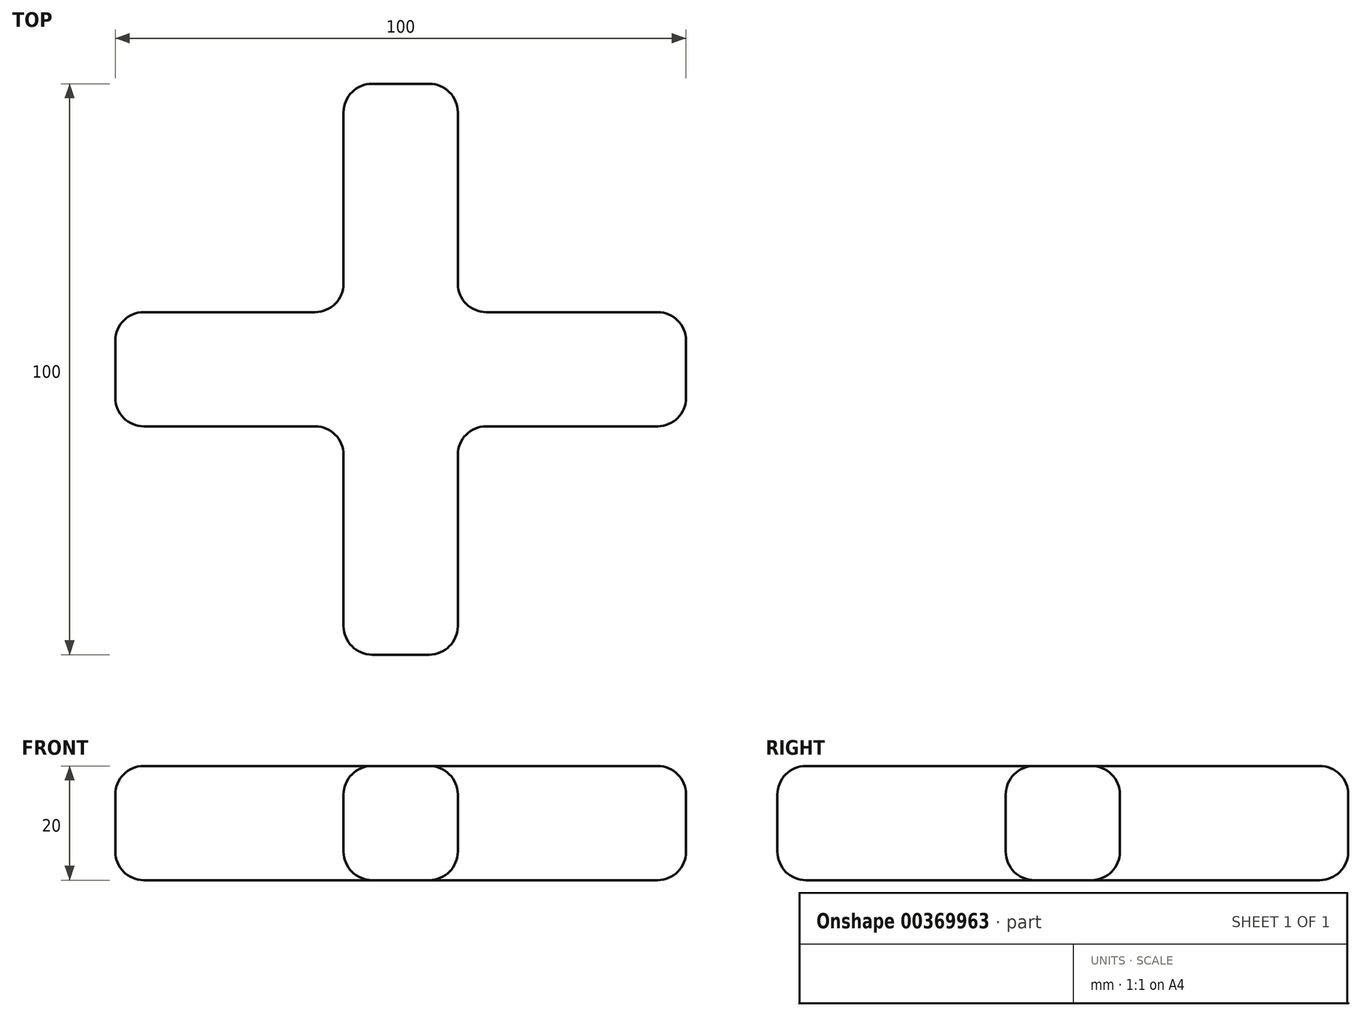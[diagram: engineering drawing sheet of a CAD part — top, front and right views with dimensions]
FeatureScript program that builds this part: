
annotation { "Feature Type Name" : "Feature", "Feature Type Description" : "" }
export const myFeature = defineFeature(function(context is Context, id is Id, definition is map)
    precondition{}
    {
        {
            var Q0;
            Q0=qCreatedBy(makeId("Top.planeOp"),FACE);
            var sketch = newSketch(context, id + "F0", { "sketchPlane" : qUnion([Q0])});
            skLineSegment(sketch, "E0.bottom", {"start": v(5, -50) * mm, "end": v(-5, -50) * mm});
            skLineSegment(sketch, "E0.top", {"start": v(5, 50) * mm, "end": v(-5, 50) * mm});
            skLineSegment(sketch, "E0.left", {"start": v(10, -45) * mm, "end": v(10, -15) * mm});
            skLineSegment(sketch, "E0.right", {"start": v(-10, 15) * mm, "end": v(-10, 45) * mm});
            skPoint(sketch, "E0.middle", {"position": v(0, 0) * mm});
            skLineSegment(sketch, "E1.bottom", {"start": v(15, -10) * mm, "end": v(45, -10) * mm});
            skLineSegment(sketch, "E1.top", {"start": v(-45, 10) * mm, "end": v(-15, 10) * mm});
            skLineSegment(sketch, "E1.left", {"start": v(-50, -5) * mm, "end": v(-50, 5) * mm});
            skLineSegment(sketch, "E1.right", {"start": v(50, -5) * mm, "end": v(50, 5) * mm});
            skPoint(sketch, "E2.newPointA", {"position": v(50, 10) * mm});
            skArc(sketch, "E2.filletArc", {"start": v(-15, 10) * mm, "mid": v(-11.46, 11.46) * mm, "end": v(-10, 15) * mm});
            skPoint(sketch, "E3.newPointA", {"position": v(-50, -10) * mm});
            skPoint(sketch, "E3.newPointB", {"position": v(10, 50) * mm});
            skArc(sketch, "E3.filletArc", {"start": v(15, -10) * mm, "mid": v(11.46, -11.46) * mm, "end": v(10, -15) * mm});
            skLineSegment(sketch, "E4", {"start": v(10, 45) * mm, "end": v(10, 15) * mm});
            skLineSegment(sketch, "E5", {"start": v(15, 10) * mm, "end": v(45, 10) * mm});
            skLineSegment(sketch, "E6", {"start": v(-45, -10) * mm, "end": v(-15, -10) * mm});
            skLineSegment(sketch, "E7", {"start": v(-10, -15) * mm, "end": v(-10, -45) * mm});
            skPoint(sketch, "E8.visualSharp", {"position": v(-10, -10) * mm});
            skArc(sketch, "E8.filletArc", {"start": v(-10, -15) * mm, "mid": v(-11.46, -11.46) * mm, "end": v(-15, -10) * mm});
            skPoint(sketch, "E9.visualSharp", {"position": v(10, 10) * mm});
            skArc(sketch, "E9.filletArc", {"start": v(10, 15) * mm, "mid": v(11.46, 11.46) * mm, "end": v(15, 10) * mm});
            skArc(sketch, "E10.filletArc", {"start": v(50, 5) * mm, "mid": v(48.54, 8.54) * mm, "end": v(45, 10) * mm});
            skPoint(sketch, "E11.visualSharp", {"position": v(50, -10) * mm});
            skArc(sketch, "E11.filletArc", {"start": v(45, -10) * mm, "mid": v(48.54, -8.54) * mm, "end": v(50, -5) * mm});
            skPoint(sketch, "E12.visualSharp", {"position": v(10, -50) * mm});
            skArc(sketch, "E12.filletArc", {"start": v(5, -50) * mm, "mid": v(8.54, -48.54) * mm, "end": v(10, -45) * mm});
            skPoint(sketch, "E13.visualSharp", {"position": v(-10, -50) * mm});
            skArc(sketch, "E13.filletArc", {"start": v(-10, -45) * mm, "mid": v(-8.54, -48.54) * mm, "end": v(-5, -50) * mm});
            skArc(sketch, "E14.filletArc", {"start": v(-50, -5) * mm, "mid": v(-48.54, -8.54) * mm, "end": v(-45, -10) * mm});
            skPoint(sketch, "E15.visualSharp", {"position": v(-50, 10) * mm});
            skArc(sketch, "E15.filletArc", {"start": v(-45, 10) * mm, "mid": v(-48.54, 8.54) * mm, "end": v(-50, 5) * mm});
            skPoint(sketch, "E16.visualSharp", {"position": v(-10, 50) * mm});
            skArc(sketch, "E16.filletArc", {"start": v(-5, 50) * mm, "mid": v(-8.54, 48.54) * mm, "end": v(-10, 45) * mm});
            skArc(sketch, "E17.filletArc", {"start": v(10, 45) * mm, "mid": v(8.54, 48.54) * mm, "end": v(5, 50) * mm});
            skSolve(sketch);
        }
        {
            var Q0;
            Q0 = qSketchRegion(id + "F0", true);
            extrude(context, id + "F1", {"entities" : qUnion([Q0]), "endBound" : BoundingType.SYMMETRIC, "depth" : 20 * mm});
        }
        {
            var Q0;
            Q0=makeQuery(id+"F1.opExtrude","CAP_FACE",FACE,{"disambiguationData":[OSD([sQuery(id+"F0.wireOp",EDGE,"E0.bottom"),sQuery(id+"F0.wireOp",EDGE,"E0.top"),sQuery(id+"F0.wireOp",EDGE,"E0.left"),sQuery(id+"F0.wireOp",EDGE,"E0.right"),sQuery(id+"F0.wireOp",EDGE,"E1.bottom"),sQuery(id+"F0.wireOp",EDGE,"E1.top"),sQuery(id+"F0.wireOp",EDGE,"E1.left"),sQuery(id+"F0.wireOp",EDGE,"E1.right"),sQuery(id+"F0.wireOp",EDGE,"E2.filletArc"),sQuery(id+"F0.wireOp",EDGE,"E3.filletArc"),sQuery(id+"F0.wireOp",EDGE,"E4"),sQuery(id+"F0.wireOp",EDGE,"E5"),sQuery(id+"F0.wireOp",EDGE,"E6"),sQuery(id+"F0.wireOp",EDGE,"E7"),sQuery(id+"F0.wireOp",EDGE,"E8.filletArc"),sQuery(id+"F0.wireOp",EDGE,"E9.filletArc"),sQuery(id+"F0.wireOp",EDGE,"E10.filletArc"),sQuery(id+"F0.wireOp",EDGE,"E11.filletArc"),sQuery(id+"F0.wireOp",EDGE,"E12.filletArc"),sQuery(id+"F0.wireOp",EDGE,"E13.filletArc"),sQuery(id+"F0.wireOp",EDGE,"E14.filletArc"),sQuery(id+"F0.wireOp",EDGE,"E15.filletArc"),sQuery(id+"F0.wireOp",EDGE,"E16.filletArc"),sQuery(id+"F0.wireOp",EDGE,"E17.filletArc")])],"isStart":false});
            var Q1;
            Q1=makeQuery(id+"F1.opExtrude","CAP_FACE",FACE,{"disambiguationData":[OSD([sQuery(id+"F0.wireOp",EDGE,"E0.bottom"),sQuery(id+"F0.wireOp",EDGE,"E0.top"),sQuery(id+"F0.wireOp",EDGE,"E0.left"),sQuery(id+"F0.wireOp",EDGE,"E0.right"),sQuery(id+"F0.wireOp",EDGE,"E1.bottom"),sQuery(id+"F0.wireOp",EDGE,"E1.top"),sQuery(id+"F0.wireOp",EDGE,"E1.left"),sQuery(id+"F0.wireOp",EDGE,"E1.right"),sQuery(id+"F0.wireOp",EDGE,"E2.filletArc"),sQuery(id+"F0.wireOp",EDGE,"E3.filletArc"),sQuery(id+"F0.wireOp",EDGE,"E4"),sQuery(id+"F0.wireOp",EDGE,"E5"),sQuery(id+"F0.wireOp",EDGE,"E6"),sQuery(id+"F0.wireOp",EDGE,"E7"),sQuery(id+"F0.wireOp",EDGE,"E8.filletArc"),sQuery(id+"F0.wireOp",EDGE,"E9.filletArc"),sQuery(id+"F0.wireOp",EDGE,"E10.filletArc"),sQuery(id+"F0.wireOp",EDGE,"E11.filletArc"),sQuery(id+"F0.wireOp",EDGE,"E12.filletArc"),sQuery(id+"F0.wireOp",EDGE,"E13.filletArc"),sQuery(id+"F0.wireOp",EDGE,"E14.filletArc"),sQuery(id+"F0.wireOp",EDGE,"E15.filletArc"),sQuery(id+"F0.wireOp",EDGE,"E16.filletArc"),sQuery(id+"F0.wireOp",EDGE,"E17.filletArc")])],"isStart":true});
            fillet(context, id + "F2", {"entities" : qUnion([Q0, Q1]), "radius" : 5 * mm, "tangentPropagation" : true, "allowEdgeOverflow" : false});
        }
    });
